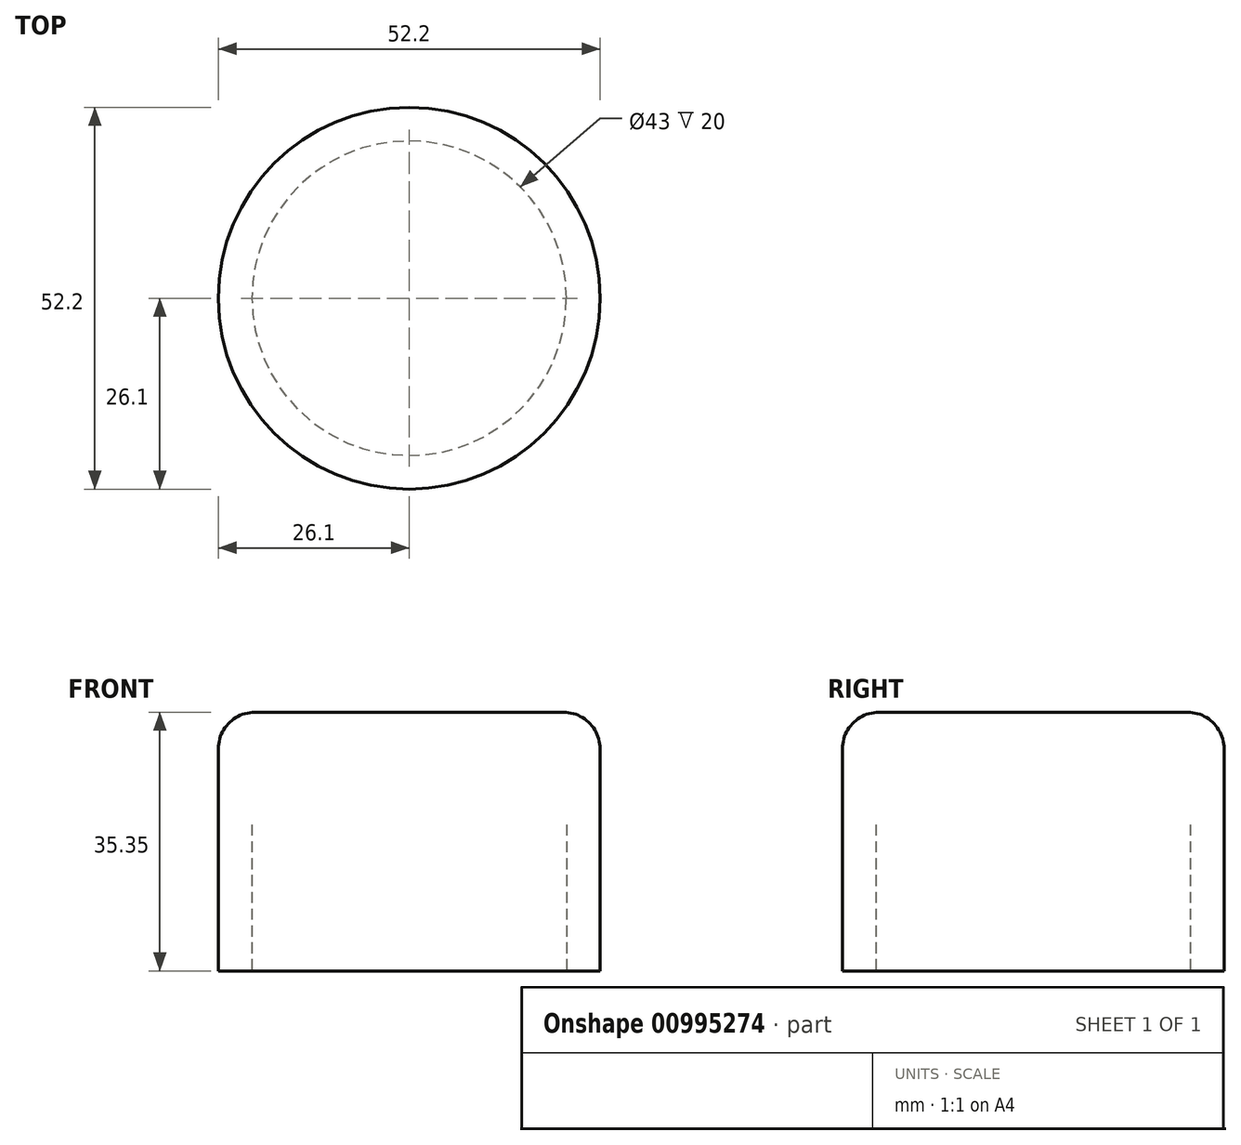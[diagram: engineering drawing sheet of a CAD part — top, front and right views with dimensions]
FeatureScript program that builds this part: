
annotation { "Feature Type Name" : "Feature", "Feature Type Description" : "" }
export const myFeature = defineFeature(function(context is Context, id is Id, definition is map)
    precondition{}
    {
        {
            var Q0;
            Q0=qCreatedBy(makeId("Front.planeOp"),FACE);
            var sketch = newSketch(context, id + "F0", { "sketchPlane" : qUnion([Q0])});
            skPoint(sketch, "E0", {"position": v(21.5, 0) * mm});
            skLineSegment(sketch, "E1", {"start": v(21.5, 0) * mm, "end": v(21.5, 20) * mm});
            skArc(sketch, "E2", {"start": v(21.5, 20) * mm, "mid": v(10.75, 30.75) * mm, "end": v(0, 20) * mm});
            skPoint(sketch, "E3", {"position": v(26.1, 0) * mm});
            skLineSegment(sketch, "E4", {"start": v(26.1, 0) * mm, "end": v(26.1, 35.35) * mm});
            skLineSegment(sketch, "E5", {"start": v(26.1, 35.35) * mm, "end": v(0, 35.35) * mm});
            skLineSegment(sketch, "E6", {"start": v(0, 35.35) * mm, "end": v(0, 20) * mm});
            skLineSegment(sketch, "E7", {"start": v(26.1, 0) * mm, "end": v(21.5, 0) * mm});
            skLineSegment(sketch, "E8", {"start": v(0, 0) * mm, "end": v(0, 20) * mm, "construction": true});
            skSolve(sketch);
        }
        {
            var Q0;
            Q0 = qSketchRegion(id + "F0", true);
            var Q1;
            Q1=sQuery(id+"F0.wireOp",EDGE,"E8");
            revolve(context, id + "F1", {"surfaceOperationType" : NewSurfaceOperationType.NEW, "entities" : qUnion([Q0]), "axis" : qUnion([Q1]), "revolveType" : RevolveType.FULL});
        }
        {
            var Q0;
            Q0=makeQuery(id+"F1.opRevolve","SWEPT_EDGE",EDGE,{"disambiguationData":[OSD([sQuery(id+"F0.wireOp",EDGE,"E4"),sQuery(id+"F0.wireOp",EDGE,"E5")])]});
            fillet(context, id + "F2", {"entities" : qUnion([Q0]), "radius" : 5 * mm, "tangentPropagation" : true, "allowEdgeOverflow" : false});
        }
    });
